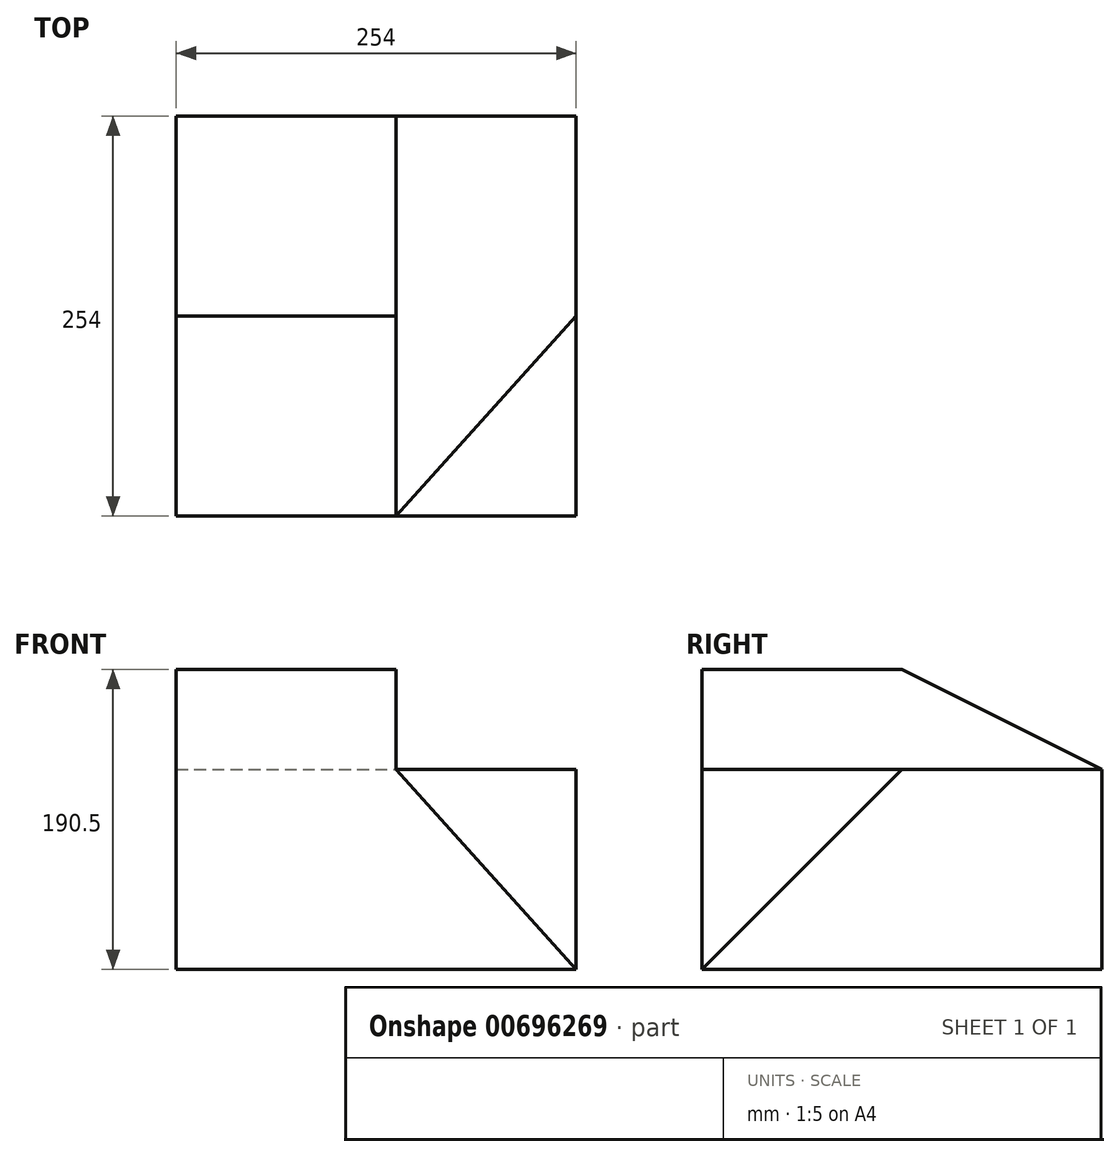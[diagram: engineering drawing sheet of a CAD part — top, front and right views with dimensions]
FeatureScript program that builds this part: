
annotation { "Feature Type Name" : "Feature", "Feature Type Description" : "" }
export const myFeature = defineFeature(function(context is Context, id is Id, definition is map)
    precondition{}
    {
        {
            var Q0;
            Q0=qCreatedBy(makeId("Top.planeOp"),FACE);
            var sketch = newSketch(context, id + "F0", { "sketchPlane" : qUnion([Q0])});
            skLineSegment(sketch, "E0.bottom", {"start": v(-127, -127) * mm, "end": v(127, -127) * mm});
            skLineSegment(sketch, "E0.top", {"start": v(-127, 127) * mm, "end": v(127, 127) * mm});
            skLineSegment(sketch, "E0.left", {"start": v(-127, -127) * mm, "end": v(-127, 127) * mm});
            skLineSegment(sketch, "E0.right", {"start": v(127, -127) * mm, "end": v(127, 127) * mm});
            skPoint(sketch, "E0.middle", {"position": v(0, 0) * mm});
            skLineSegment(sketch, "E1.0", {"start": v(-127, 0) * mm, "end": v(12.7, 0) * mm});
            skLineSegment(sketch, "E2.0", {"start": v(12.7, -127) * mm, "end": v(12.7, 127) * mm});
            skLineSegment(sketch, "E3", {"start": v(127, 0) * mm, "end": v(12.7, -127) * mm});
            skSolve(sketch);
        }
        {
            var Q0;
            Q0=qCreatedBy(makeId("Right.planeOp"),FACE);
            var sketch = newSketch(context, id + "F1", { "sketchPlane" : qUnion([Q0])});
            skLineSegment(sketch, "E4.top", {"start": v(127, -95.25) * mm, "end": v(-127, -95.25) * mm});
            skLineSegment(sketch, "E4.left", {"start": v(127, 31.75) * mm, "end": v(127, -95.25) * mm});
            skLineSegment(sketch, "E4.right", {"start": v(-127, 31.75) * mm, "end": v(-127, -95.25) * mm});
            skPoint(sketch, "E4.middle", {"position": v(0, 0) * mm});
            skLineSegment(sketch, "E5.0", {"start": v(254, 95.25) * mm, "end": v(254, -95.25) * mm});
            skLineSegment(sketch, "E6.0", {"start": v(127, 31.75) * mm, "end": v(-127, 31.75) * mm});
            skPoint(sketch, "E7.orphan", {"position": v(-127, 95.25) * mm});
            skLineSegment(sketch, "E8", {"start": v(0, 95.25) * mm, "end": v(-127, 95.25) * mm});
            skLineSegment(sketch, "E9", {"start": v(-127, 31.75) * mm, "end": v(-127, 95.25) * mm});
            skLineSegment(sketch, "E10", {"start": v(0, 31.75) * mm, "end": v(-127, -95.25) * mm});
            skLineSegment(sketch, "E11", {"start": v(127, 31.75) * mm, "end": v(0, 95.25) * mm});
            skPoint(sketch, "E12.orphan", {"position": v(127, 95.25) * mm});
            skLineSegment(sketch, "E13", {"start": v(0, 31.75) * mm, "end": v(0, -95.25) * mm});
            skSolve(sketch);
        }
        {
            var Q0;
            Q0=makeQuery(id+"F1.imprint","IMPRINT",FACE,{"disambiguationData":[TD([[makeQuery(id+"F1.imprint","IMPRINT",EDGE,{"derivedFrom":sQuery(id+"F1.wireOp",EDGE,"E8")}),1.0]])]});
            extrude(context, id + "F2", {"entities" : qUnion([Q0]), "oppositeDirection" : true, "depth" : 127 * mm, "offsetDistance" : 25.4 * mm});
        }
        {
            var Q0;
            Q0=makeQuery(id+"F1.imprint","IMPRINT",FACE,{"disambiguationData":[TD([[makeQuery(id+"F1.imprint","IMPRINT",EDGE,{"derivedFrom":sQuery(id+"F1.wireOp",EDGE,"E8")}),1.0]])]});
            extrude(context, id + "F3", {"entities" : qUnion([Q0]), "operationType" : NewBodyOperationType.ADD, "depth" : 12.7 * mm, "offsetDistance" : 25.4 * mm});
        }
        {
            var Q0;
            {var subQ5=sQuery(id+"F0.wireOp",EDGE,"E1.0");Q0=makeQuery(id+"F0.imprint","IMPRINT",FACE,{"disambiguationData":[TD([[makeQuery(id+"F0.imprint","IMPRINT",EDGE,{"derivedFrom":subQ5}),-1.0]])]});}
            var Q1;
            {var subQ5=sQuery(id+"F0.wireOp",EDGE,"E1.0");Q1=makeQuery(id+"F0.imprint","IMPRINT",FACE,{"disambiguationData":[TD([[makeQuery(id+"F0.imprint","IMPRINT",EDGE,{"derivedFrom":subQ5}),1.0]])]});}
            extrude(context, id + "F4", {"entities" : qUnion([Q0, Q1]), "operationType" : NewBodyOperationType.ADD, "depth" : 31.75 * mm, "offsetDistance" : 25.4 * mm});
        }
        {
            var Q0;
            {var subQ5=sQuery(id+"F0.wireOp",EDGE,"E1.0");Q0=makeQuery(id+"F0.imprint","IMPRINT",FACE,{"disambiguationData":[TD([[makeQuery(id+"F0.imprint","IMPRINT",EDGE,{"derivedFrom":subQ5}),-1.0]])]});}
            var Q1;
            {var subQ5=sQuery(id+"F0.wireOp",EDGE,"E1.0");Q1=makeQuery(id+"F0.imprint","IMPRINT",FACE,{"disambiguationData":[TD([[makeQuery(id+"F0.imprint","IMPRINT",EDGE,{"derivedFrom":subQ5}),1.0]])]});}
            extrude(context, id + "F5", {"entities" : qUnion([Q0, Q1]), "operationType" : NewBodyOperationType.ADD, "oppositeDirection" : true, "depth" : 95.25 * mm, "offsetDistance" : 25.4 * mm});
        }
        {
            var Q0;
            {var subQ4=sQuery(id+"F0.wireOp",EDGE,"E3");Q0=makeQuery(id+"F0.imprint","IMPRINT",FACE,{"disambiguationData":[TD([[makeQuery(id+"F0.imprint","IMPRINT",EDGE,{"derivedFrom":subQ4}),-1.0]])]});}
            extrude(context, id + "F6", {"entities" : qUnion([Q0]), "operationType" : NewBodyOperationType.ADD, "depth" : 31.75 * mm, "offsetDistance" : 25.4 * mm});
        }
        {
            var Q0;
            {var subQ4=sQuery(id+"F0.wireOp",EDGE,"E3");Q0=makeQuery(id+"F0.imprint","IMPRINT",FACE,{"disambiguationData":[TD([[makeQuery(id+"F0.imprint","IMPRINT",EDGE,{"derivedFrom":subQ4}),-1.0]])]});}
            extrude(context, id + "F7", {"entities" : qUnion([Q0]), "operationType" : NewBodyOperationType.ADD, "oppositeDirection" : true, "depth" : 95.25 * mm, "offsetDistance" : 25.4 * mm});
        }
        {
            var Q0;
            Q0 = qSketchRegion(id + "F0", true);
            extrude(context, id + "F8", {"entities" : qUnion([Q0]), "operationType" : NewBodyOperationType.ADD, "depth" : 31.75 * mm, "offsetDistance" : 25.4 * mm});
        }
        {
            var Q0;
            {var subQ3=sQuery(id+"F0.wireOp",EDGE,"E3");Q0=makeQuery(id+"F0.imprint","IMPRINT",FACE,{"disambiguationData":[TD([[makeQuery(id+"F0.imprint","IMPRINT",EDGE,{"derivedFrom":subQ3}),1.0]])]});}
            extrude(context, id + "F9", {"entities" : qUnion([Q0]), "operationType" : NewBodyOperationType.ADD, "oppositeDirection" : true, "depth" : 95.25 * mm, "offsetDistance" : 25.4 * mm});
        }
        {
            var Q0;
            {var subQ0=sQuery(id+"F0.wireOp",EDGE,"E0.right");Q0=makeQuery(id+"F8.boolean.opBoolean","MERGE",EDGE,{"derivedFrom":[makeQuery(id+"F6.opExtrude","CAP_EDGE",EDGE,{"disambiguationData":[OSD([subQ0])],"isStart":false}),makeQuery(id+"F8.opExtrude","CAP_EDGE",EDGE,{"disambiguationData":[OSD([subQ0])],"isStart":false})]});}
            cPoint(context, id + "F10", {"entities" : qUnion([Q0]), "parameter" : 0.5});
        }
        {
            var Q0;
            Q0=makeQuery(id+"F6.opExtrude","CAP_VERTEX",VERTEX,{"disambiguationData":[OSD([sQuery(id+"F0.wireOp",EDGE,"E0.bottom"),sQuery(id+"F0.wireOp",EDGE,"E2.0"),sQuery(id+"F0.wireOp",EDGE,"E3")])],"isStart":false});
            var Q1;
            Q1 = qCreatedBy(id + "F10" ,VERTEX);
            var Q2;
            Q2=makeQuery(id+"F9.opExtrude","CAP_VERTEX",VERTEX,{"disambiguationData":[OSD([sQuery(id+"F0.wireOp",EDGE,"E0.bottom"),sQuery(id+"F0.wireOp",EDGE,"E0.right")])],"isStart":false});
            cPlane(context, id + "F11", {"entities" : qUnion([Q0, Q1, Q2]), "cplaneType" : CPlaneType.THREE_POINT, "offset" : 25.4 * mm, "width" : 152.4 * mm, "height" : 152.4 * mm});
        }
        {
            var Q0;
            Q0=qCreatedBy(id+"F11.planeOp",FACE);
            var sketch = newSketch(context, id + "F12", { "sketchPlane" : qUnion([Q0])});
            skLineSegment(sketch, "E14", {"start": v(64.3, -61.36) * mm, "end": v(-88.5, 15.1) * mm});
            skLineSegment(sketch, "E15", {"start": v(64.3, -61.36) * mm, "end": v(-88.5, -155.76) * mm});
            skLineSegment(sketch, "E16", {"start": v(-88.5, -155.76) * mm, "end": v(-88.5, 15.1) * mm});
            skSolve(sketch);
        }
        {
            var Q0;
            Q0 = qSketchRegion(id + "F12", true);
            extrude(context, id + "F13", {"entities" : qUnion([Q0]), "operationType" : NewBodyOperationType.REMOVE, "depth" : 185.67 * mm, "offsetDistance" : 25.4 * mm});
        }
    });
